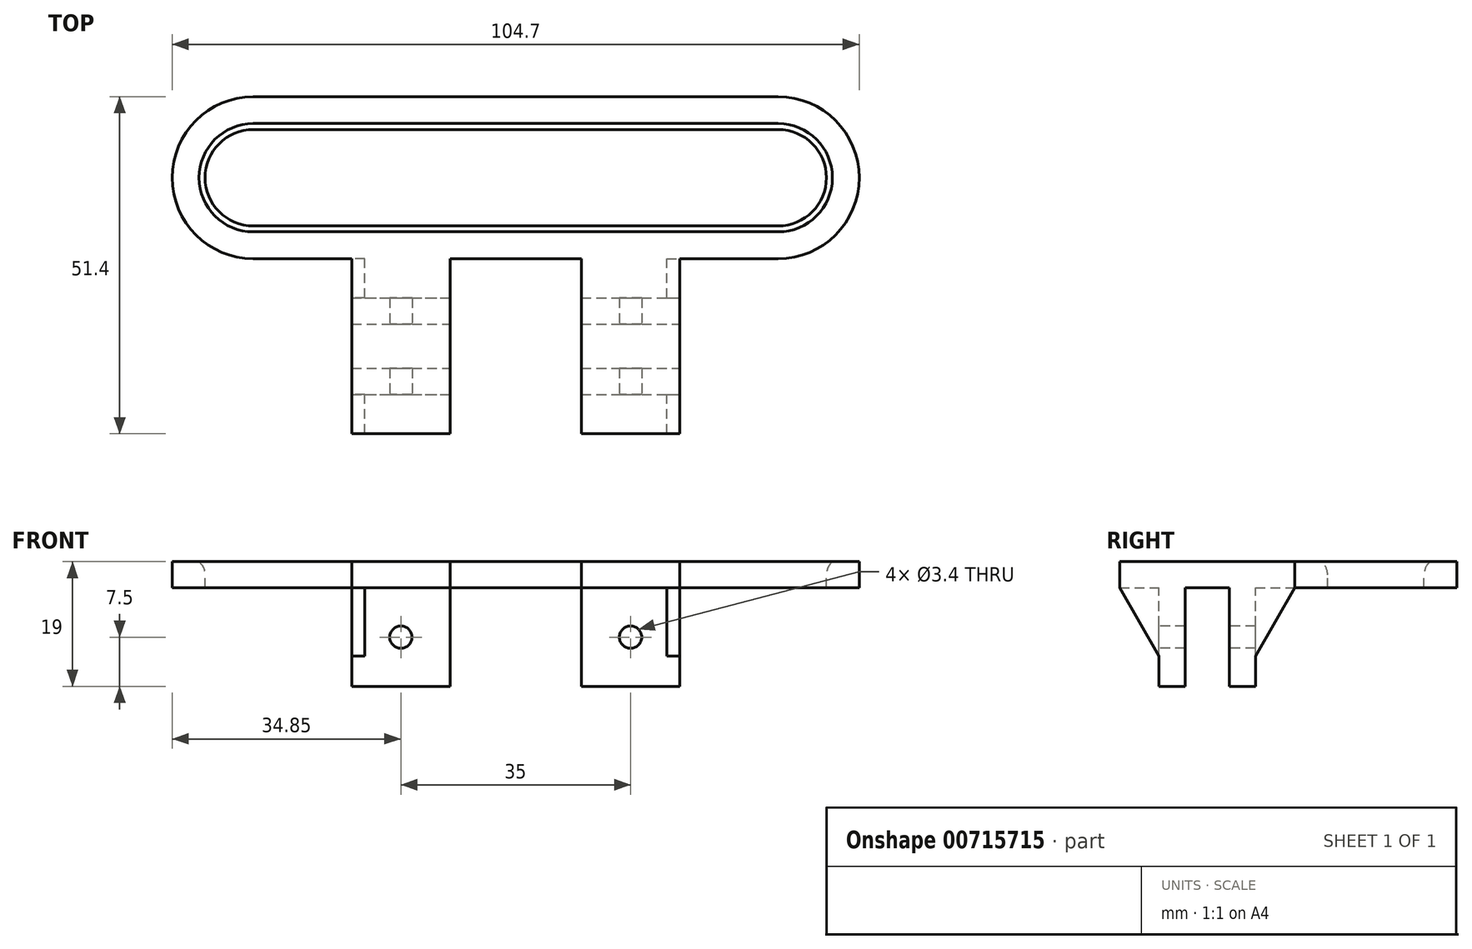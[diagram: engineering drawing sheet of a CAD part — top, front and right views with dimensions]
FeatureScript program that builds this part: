
annotation { "Feature Type Name" : "Feature", "Feature Type Description" : "" }
export const myFeature = defineFeature(function(context is Context, id is Id, definition is map)
    precondition{}
    {
        {
            var Q0;
            Q0=qCreatedBy(makeId("Top.planeOp"),FACE);
            var sketch = newSketch(context, id + "F0", { "sketchPlane" : qUnion([Q0])});
            skArc(sketch, "E0", {"start": v(-40, 26.85) * mm, "mid": v(-50, 16.85) * mm, "end": v(-40, 6.85) * mm});
            skArc(sketch, "E1", {"start": v(40, 26.85) * mm, "mid": v(50, 16.85) * mm, "end": v(40, 6.85) * mm});
            skLineSegment(sketch, "E2", {"start": v(-40, 26.85) * mm, "end": v(40, 26.85) * mm});
            skLineSegment(sketch, "E3", {"start": v(-40, 6.85) * mm, "end": v(40, 6.85) * mm});
            skSolve(sketch);
        }
        {
            var Q0;
            Q0=qCreatedBy(makeId("Right.planeOp"),FACE);
            var sketch = newSketch(context, id + "F1", { "sketchPlane" : qUnion([Q0])});
            skLineSegment(sketch, "E4", {"start": v(4.5, -2) * mm, "end": v(9.5, -2) * mm});
            skLineSegment(sketch, "E5", {"start": v(4.5, -2) * mm, "end": v(4.5, 2) * mm});
            skLineSegment(sketch, "E6.0", {"start": v(26.85, 0) * mm, "end": v(6.85, 0) * mm});
            skPoint(sketch, "E7.0", {"position": v(6.85, 0) * mm});
            skArc(sketch, "E8", {"start": v(9.5, 0) * mm, "mid": v(9.3, 1.01) * mm, "end": v(8.72, 1.87) * mm});
            skLineSegment(sketch, "E9", {"start": v(9.5, -2) * mm, "end": v(9.5, 0) * mm});
            skLineSegment(sketch, "E10", {"start": v(4.5, 2) * mm, "end": v(8.6, 2) * mm});
            skLineSegment(sketch, "E11", {"start": v(8.6, 2) * mm, "end": v(8.72, 1.87) * mm});
            skSolve(sketch);
        }
        {
            var Q0;
            Q0 = qSketchRegion(id + "F1", true);
            var Q1;
            Q1 = qConstructionFilter(qBodyType(qCreatedBy(id + "F0" ,EDGE), BodyType.WIRE), ConstructionObject.NO);
            sweep(context, id + "F2", {"profiles" : qUnion([Q0]), "path" : qUnion([Q1])});
        }
        {
            var Q0;
            Q0=makeQuery(id+"F2.opSweep","SWEPT_FACE",FACE,{"disambiguationData":[OSD([sQuery(id+"F0.wireOp",EDGE,"E3"),sQuery(id+"F1.wireOp",EDGE,"E5")])]});
            var sketch = newSketch(context, id + "F3", { "sketchPlane" : qUnion([Q0])});
            skLineSegment(sketch, "E12.bottom", {"start": v(-25, 2) * mm, "end": v(-10, 2) * mm});
            skLineSegment(sketch, "E12.top", {"start": v(-25, -2) * mm, "end": v(-10, -2) * mm});
            skLineSegment(sketch, "E12.left", {"start": v(-25, 2) * mm, "end": v(-25, -2) * mm});
            skLineSegment(sketch, "E12.right", {"start": v(-10, 2) * mm, "end": v(-10, -2) * mm});
            skLineSegment(sketch, "E13.bottom", {"start": v(10, 2) * mm, "end": v(25, 2) * mm});
            skLineSegment(sketch, "E13.top", {"start": v(10, -2) * mm, "end": v(25, -2) * mm});
            skLineSegment(sketch, "E13.left", {"start": v(10, 2) * mm, "end": v(10, -2) * mm});
            skLineSegment(sketch, "E13.right", {"start": v(25, 2) * mm, "end": v(25, -2) * mm});
            skSolve(sketch);
        }
        {
            var Q0;
            Q0 = qSketchRegion(id + "F3", true);
            extrude(context, id + "F4", {"entities" : qUnion([Q0]), "operationType" : NewBodyOperationType.ADD, "depth" : 26.7 * mm, "offsetDistance" : 25 * mm});
        }
        {
            var Q0;
            Q0=makeQuery(id+"F4.boolean.opBoolean","MERGE",FACE,{"derivedFrom":[makeQuery(id+"F2.opSweep","SWEPT_FACE",FACE,{"disambiguationData":[OSD([sQuery(id+"F0.wireOp",EDGE,"E1"),sQuery(id+"F1.wireOp",EDGE,"E4")])]}),makeQuery(id+"F4.opExtrude","SWEPT_FACE",FACE,{"disambiguationData":[OSD([sQuery(id+"F3.wireOp",EDGE,"E12.top")])]}),makeQuery(id+"F4.opExtrude","SWEPT_FACE",FACE,{"disambiguationData":[OSD([sQuery(id+"F3.wireOp",EDGE,"E13.top")])]})]});
            var sketch = newSketch(context, id + "F5", { "sketchPlane" : qUnion([Q0])});
            skLineSegment(sketch, "E14.bottom", {"start": v(-25, 16.2) * mm, "end": v(-10, 16.2) * mm});
            skLineSegment(sketch, "E14.top", {"start": v(-25, 12.2) * mm, "end": v(-10, 12.2) * mm});
            skLineSegment(sketch, "E14.left", {"start": v(-25, 16.2) * mm, "end": v(-25, 12.2) * mm});
            skLineSegment(sketch, "E14.right", {"start": v(-10, 16.2) * mm, "end": v(-10, 12.2) * mm});
            skLineSegment(sketch, "E15", {"start": v(-25, 5.5) * mm, "end": v(-10, 5.5) * mm});
            skLineSegment(sketch, "E16", {"start": v(-25, 5.5) * mm, "end": v(-25, 1.5) * mm});
            skLineSegment(sketch, "E17", {"start": v(-25, 1.5) * mm, "end": v(-10, 1.5) * mm});
            skLineSegment(sketch, "E18", {"start": v(-10, 1.5) * mm, "end": v(-10, 5.5) * mm});
            skLineSegment(sketch, "E19.bottom", {"start": v(10, 16.2) * mm, "end": v(25, 16.2) * mm});
            skLineSegment(sketch, "E19.top", {"start": v(10, 12.2) * mm, "end": v(25, 12.2) * mm});
            skLineSegment(sketch, "E19.left", {"start": v(10, 16.2) * mm, "end": v(10, 12.2) * mm});
            skLineSegment(sketch, "E19.right", {"start": v(25, 16.2) * mm, "end": v(25, 12.2) * mm});
            skLineSegment(sketch, "E20.bottom", {"start": v(10, 5.5) * mm, "end": v(25, 5.5) * mm});
            skLineSegment(sketch, "E20.top", {"start": v(10, 1.5) * mm, "end": v(25, 1.5) * mm});
            skLineSegment(sketch, "E20.left", {"start": v(10, 5.5) * mm, "end": v(10, 1.5) * mm});
            skLineSegment(sketch, "E20.right", {"start": v(25, 5.5) * mm, "end": v(25, 1.5) * mm});
            skSolve(sketch);
        }
        {
            var Q0;
            Q0 = qSketchRegion(id + "F5", true);
            extrude(context, id + "F6", {"entities" : qUnion([Q0]), "operationType" : NewBodyOperationType.ADD, "depth" : 15 * mm, "offsetDistance" : 25 * mm});
        }
        {
            var Q0;
            Q0=makeQuery(id+"F6.opExtrude","SWEPT_FACE",FACE,{"disambiguationData":[OSD([sQuery(id+"F5.wireOp",EDGE,"E14.bottom")])]});
            var sketch = newSketch(context, id + "F7", { "sketchPlane" : qUnion([Q0])});
            skCircle(sketch, "E21", {"center": v(-17.5, -9.5) * mm, "radius": 1.7 * mm});
            skCircle(sketch, "E22", {"center": v(17.5, -9.5) * mm, "radius": 1.7 * mm});
            skSolve(sketch);
        }
        {
            var Q0;
            Q0 = qSketchRegion(id + "F7", true);
            extrude(context, id + "F8", {"entities" : qUnion([Q0]), "operationType" : NewBodyOperationType.REMOVE, "endBound" : BoundingType.THROUGH_ALL, "oppositeDirection" : true, "depth" : 25 * mm, "offsetDistance" : 25 * mm});
        }
        {
            var Q0;
            Q0=makeQuery(id+"F6.boolean.opBoolean","MERGE",FACE,{"derivedFrom":[makeQuery(id+"F4.opExtrude","SWEPT_FACE",FACE,{"disambiguationData":[OSD([sQuery(id+"F3.wireOp",EDGE,"E12.left")])]}),makeQuery(id+"F6.opExtrude","SWEPT_FACE",FACE,{"disambiguationData":[OSD([sQuery(id+"F5.wireOp",EDGE,"E14.left")])]}),makeQuery(id+"F6.opExtrude","SWEPT_FACE",FACE,{"disambiguationData":[OSD([sQuery(id+"F5.wireOp",EDGE,"E16")])]})]});
            var sketch = newSketch(context, id + "F9", { "sketchPlane" : qUnion([Q0])});
            skPoint(sketch, "E23.0", {"position": v(1.5, -2) * mm});
            skPoint(sketch, "E24.0", {"position": v(16.2, -2) * mm});
            skLineSegment(sketch, "E25", {"start": v(1.5, -2) * mm, "end": v(-4.5, -2) * mm});
            skLineSegment(sketch, "E26", {"start": v(-4.5, -2) * mm, "end": v(1.5, -12.4) * mm});
            skLineSegment(sketch, "E27", {"start": v(1.5, -12.4) * mm, "end": v(1.5, -2) * mm});
            skLineSegment(sketch, "E28", {"start": v(16.2, -2) * mm, "end": v(22.2, -2) * mm});
            skLineSegment(sketch, "E29", {"start": v(22.2, -2) * mm, "end": v(16.2, -12.4) * mm});
            skLineSegment(sketch, "E30", {"start": v(16.2, -12.4) * mm, "end": v(16.2, -2) * mm});
            skSolve(sketch);
        }
        {
            var Q0;
            Q0 = qSketchRegion(id + "F9", true);
            extrude(context, id + "F10", {"entities" : qUnion([Q0]), "operationType" : NewBodyOperationType.ADD, "oppositeDirection" : true, "depth" : 2 * mm, "offsetDistance" : 25 * mm});
        }
        {
            var Q0;
            Q0=makeQuery(id+"F6.boolean.opBoolean","MERGE",FACE,{"derivedFrom":[makeQuery(id+"F4.opExtrude","SWEPT_FACE",FACE,{"disambiguationData":[OSD([sQuery(id+"F3.wireOp",EDGE,"E13.right")])]}),makeQuery(id+"F6.opExtrude","SWEPT_FACE",FACE,{"disambiguationData":[OSD([sQuery(id+"F5.wireOp",EDGE,"E19.right")])]}),makeQuery(id+"F6.opExtrude","SWEPT_FACE",FACE,{"disambiguationData":[OSD([sQuery(id+"F5.wireOp",EDGE,"E20.right")])]})]});
            var sketch = newSketch(context, id + "F11", { "sketchPlane" : qUnion([Q0])});
            skLineSegment(sketch, "E31", {"start": v(-16.2, -2) * mm, "end": v(-22.2, -2) * mm});
            skLineSegment(sketch, "E32", {"start": v(-22.2, -2) * mm, "end": v(-16.2, -12.4) * mm});
            skLineSegment(sketch, "E33", {"start": v(-16.2, -12.4) * mm, "end": v(-16.2, -2) * mm});
            skLineSegment(sketch, "E34", {"start": v(4.5, -2) * mm, "end": v(-1.5, -2) * mm});
            skLineSegment(sketch, "E35", {"start": v(-1.5, -2) * mm, "end": v(-1.5, -12.4) * mm});
            skLineSegment(sketch, "E36", {"start": v(-1.5, -12.4) * mm, "end": v(4.5, -2) * mm});
            skSolve(sketch);
        }
        {
            var Q0;
            Q0 = qSketchRegion(id + "F11", true);
            extrude(context, id + "F12", {"entities" : qUnion([Q0]), "operationType" : NewBodyOperationType.ADD, "oppositeDirection" : true, "depth" : 2 * mm, "offsetDistance" : 25 * mm});
        }
    });
